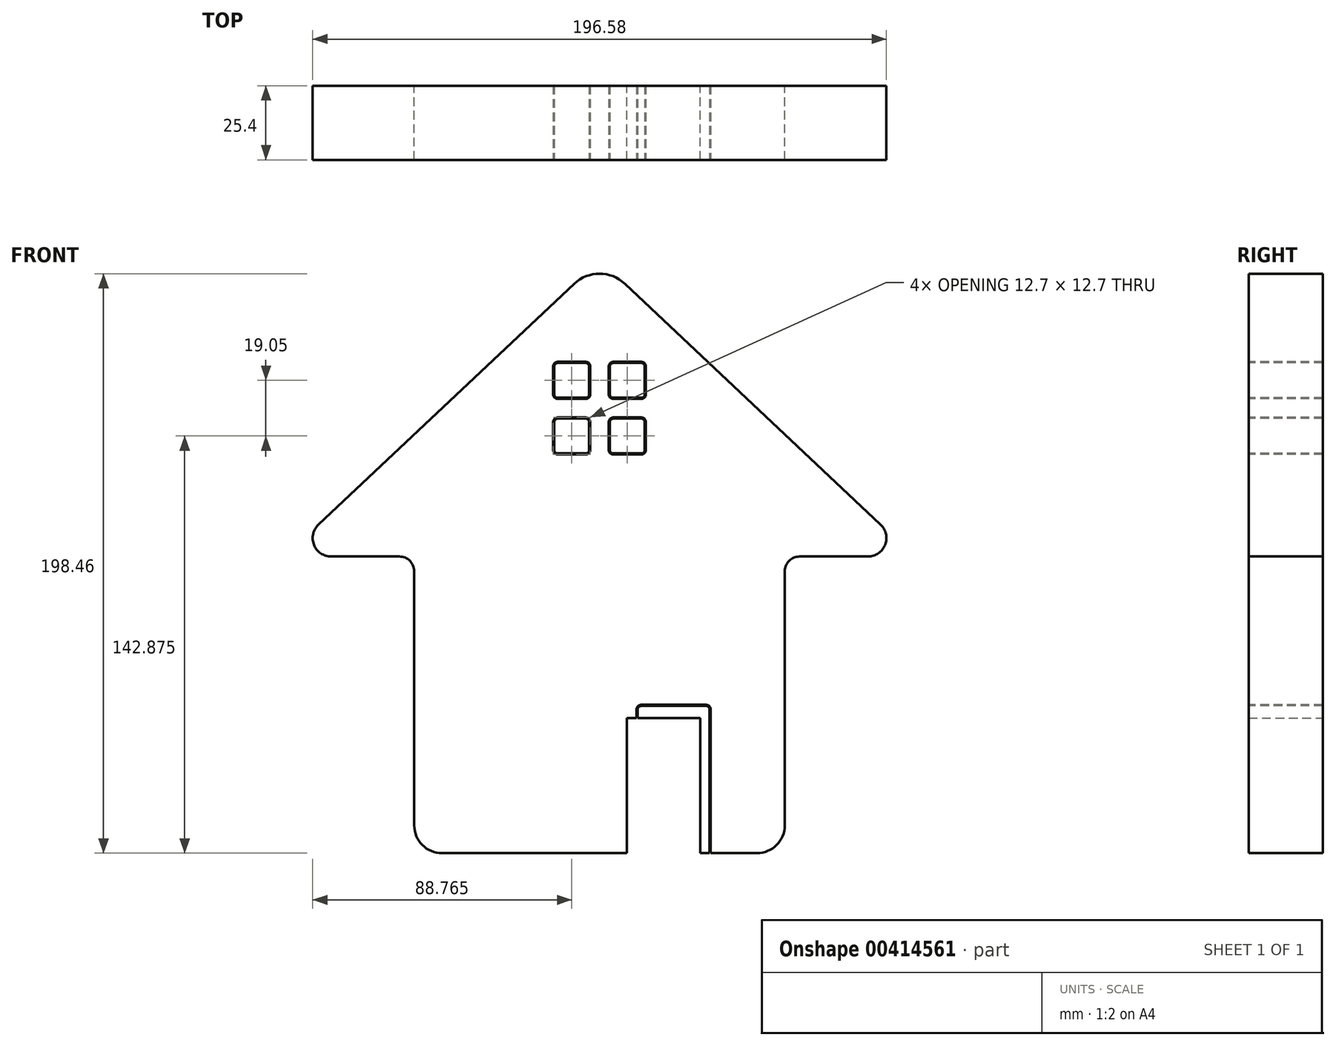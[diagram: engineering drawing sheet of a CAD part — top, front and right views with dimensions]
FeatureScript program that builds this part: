
annotation { "Feature Type Name" : "Feature", "Feature Type Description" : "" }
export const myFeature = defineFeature(function(context is Context, id is Id, definition is map)
    precondition{}
    {
        {
            var Q0;
            Q0=qCreatedBy(makeId("Front.planeOp"),FACE);
            var sketch = newSketch(context, id + "F0", { "sketchPlane" : qUnion([Q0])});
            skLineSegment(sketch, "E0.bottom", {"start": v(-63.5, 0) * mm, "end": v(63.5, 0) * mm});
            skLineSegment(sketch, "E0.top", {"start": v(-63.5, 101.6) * mm, "end": v(63.5, 101.6) * mm, "construction": true});
            skLineSegment(sketch, "E0.left", {"start": v(-63.5, 0) * mm, "end": v(-63.5, 101.6) * mm});
            skLineSegment(sketch, "E0.right", {"start": v(63.5, 0) * mm, "end": v(63.5, 101.6) * mm});
            skLineSegment(sketch, "E1", {"start": v(-63.5, 101.6) * mm, "end": v(-107.95, 101.6) * mm});
            skLineSegment(sketch, "E2", {"start": v(-107.95, 101.6) * mm, "end": v(0, 203.2) * mm});
            skLineSegment(sketch, "E3", {"start": v(0, 203.2) * mm, "end": v(107.95, 101.6) * mm});
            skLineSegment(sketch, "E4", {"start": v(107.95, 101.6) * mm, "end": v(63.5, 101.6) * mm});
            skLineSegment(sketch, "E5.bottom", {"start": v(9.41, 0) * mm, "end": v(34.5, 0) * mm});
            skLineSegment(sketch, "E5.top", {"start": v(9.41, 46.26) * mm, "end": v(34.5, 46.26) * mm});
            skLineSegment(sketch, "E5.left", {"start": v(9.41, 0) * mm, "end": v(9.41, 46.26) * mm});
            skLineSegment(sketch, "E5.right", {"start": v(34.5, 0) * mm, "end": v(34.5, 46.26) * mm});
            skSolve(sketch);
        }
        {
            var Q0;
            {var subQ1=sQuery(id+"F0.wireOp",EDGE,"E0.left");Q0=makeQuery(id+"F0.imprint","IMPRINT",FACE,{"disambiguationData":[TD([[makeQuery(id+"F0.imprint","IMPRINT",EDGE,{"derivedFrom":subQ1}),-1.0]])]});}
            var Q1;
            Q1=makeQuery(id+"F0.imprint","IMPRINT",FACE,{"disambiguationData":[TD([[makeQuery(id+"F0.imprint","IMPRINT",EDGE,{"derivedFrom":sQuery(id+"F0.wireOp",EDGE,"E5.bottom")}),1.0]])]});
            extrude(context, id + "F1", {"entities" : qUnion([Q0, Q1]), "depth" : 25.4 * mm});
        }
        {
            var Q0;
            Q0=makeQuery(id+"F1.opExtrude","CAP_FACE",FACE,{"disambiguationData":[OSD([sQuery(id+"F0.wireOp",EDGE,"E0.bottom"),sQuery(id+"F0.wireOp",EDGE,"E0.left"),sQuery(id+"F0.wireOp",EDGE,"E0.right"),sQuery(id+"F0.wireOp",EDGE,"E1"),sQuery(id+"F0.wireOp",EDGE,"E2"),sQuery(id+"F0.wireOp",EDGE,"E3"),sQuery(id+"F0.wireOp",EDGE,"E4"),sQuery(id+"F0.wireOp",EDGE,"E5.bottom")])],"isStart":false});
            var sketch = newSketch(context, id + "F2", { "sketchPlane" : qUnion([Q0])});
            skLineSegment(sketch, "E6.bottom", {"start": v(-19.05, 171.45) * mm, "end": v(19.05, 171.45) * mm, "construction": true});
            skLineSegment(sketch, "E6.top", {"start": v(-19.05, 133.35) * mm, "end": v(19.05, 133.35) * mm, "construction": true});
            skLineSegment(sketch, "E6.left", {"start": v(-19.05, 171.45) * mm, "end": v(-19.05, 133.35) * mm, "construction": true});
            skLineSegment(sketch, "E6.right", {"start": v(19.05, 171.45) * mm, "end": v(19.05, 133.35) * mm, "construction": true});
            skLineSegment(sketch, "E7", {"start": v(0, 203.2) * mm, "end": v(0, 171.45) * mm, "construction": true});
            skLineSegment(sketch, "E8.bottom", {"start": v(-14.29, 168.28) * mm, "end": v(-4.76, 168.28) * mm});
            skLineSegment(sketch, "E8.top", {"start": v(-14.29, 155.58) * mm, "end": v(-4.76, 155.58) * mm});
            skLineSegment(sketch, "E8.left", {"start": v(-15.88, 166.69) * mm, "end": v(-15.88, 157.16) * mm});
            skLineSegment(sketch, "E8.right", {"start": v(-3.18, 166.69) * mm, "end": v(-3.18, 157.16) * mm});
            skLineSegment(sketch, "E9.bottom", {"start": v(4.76, 168.28) * mm, "end": v(14.29, 168.28) * mm});
            skLineSegment(sketch, "E9.top", {"start": v(4.76, 155.58) * mm, "end": v(14.29, 155.58) * mm});
            skLineSegment(sketch, "E9.left", {"start": v(3.17, 166.69) * mm, "end": v(3.17, 157.16) * mm});
            skLineSegment(sketch, "E9.right", {"start": v(15.87, 166.69) * mm, "end": v(15.87, 157.16) * mm});
            skLineSegment(sketch, "E10.bottom", {"start": v(-14.29, 149.23) * mm, "end": v(-4.76, 149.23) * mm});
            skLineSegment(sketch, "E10.top", {"start": v(-14.29, 136.53) * mm, "end": v(-4.76, 136.53) * mm});
            skLineSegment(sketch, "E10.left", {"start": v(-15.88, 147.64) * mm, "end": v(-15.88, 138.11) * mm});
            skLineSegment(sketch, "E10.right", {"start": v(-3.18, 147.64) * mm, "end": v(-3.18, 138.11) * mm});
            skLineSegment(sketch, "E11.bottom", {"start": v(4.76, 149.23) * mm, "end": v(14.29, 149.23) * mm});
            skLineSegment(sketch, "E11.top", {"start": v(4.76, 136.53) * mm, "end": v(14.29, 136.53) * mm});
            skLineSegment(sketch, "E11.left", {"start": v(3.17, 147.64) * mm, "end": v(3.17, 138.11) * mm});
            skLineSegment(sketch, "E11.right", {"start": v(15.87, 147.64) * mm, "end": v(15.87, 138.11) * mm});
            skLineSegment(sketch, "E12", {"start": v(-3.17, 168.28) * mm, "end": v(3.17, 168.28) * mm, "construction": true});
            skLineSegment(sketch, "E13", {"start": v(0, 168.28) * mm, "end": v(0, 171.45) * mm, "construction": true});
            skLineSegment(sketch, "E14", {"start": v(-15.88, 168.28) * mm, "end": v(-15.88, 171.45) * mm});
            skLineSegment(sketch, "E15", {"start": v(-15.88, 136.53) * mm, "end": v(-15.88, 133.35) * mm});
            skPoint(sketch, "E16.visualSharp", {"position": v(-15.87, 168.28) * mm});
            skArc(sketch, "E16.filletArc", {"start": v(-14.29, 168.28) * mm, "mid": v(-15.41, 167.81) * mm, "end": v(-15.88, 166.69) * mm});
            skPoint(sketch, "E17.visualSharp", {"position": v(-3.17, 168.28) * mm});
            skArc(sketch, "E17.filletArc", {"start": v(-3.18, 166.69) * mm, "mid": v(-3.64, 167.81) * mm, "end": v(-4.76, 168.28) * mm});
            skPoint(sketch, "E18.visualSharp", {"position": v(-3.18, 155.58) * mm});
            skArc(sketch, "E18.filletArc", {"start": v(-4.76, 155.58) * mm, "mid": v(-3.64, 156.04) * mm, "end": v(-3.18, 157.16) * mm});
            skPoint(sketch, "E19.visualSharp", {"position": v(-15.88, 155.58) * mm});
            skArc(sketch, "E19.filletArc", {"start": v(-15.88, 157.16) * mm, "mid": v(-15.41, 156.04) * mm, "end": v(-14.29, 155.58) * mm});
            skPoint(sketch, "E20.visualSharp", {"position": v(3.17, 168.28) * mm});
            skArc(sketch, "E20.filletArc", {"start": v(4.76, 168.28) * mm, "mid": v(3.64, 167.81) * mm, "end": v(3.17, 166.69) * mm});
            skPoint(sketch, "E21.visualSharp", {"position": v(15.87, 168.28) * mm});
            skArc(sketch, "E21.filletArc", {"start": v(15.87, 166.69) * mm, "mid": v(15.41, 167.81) * mm, "end": v(14.29, 168.28) * mm});
            skPoint(sketch, "E22.visualSharp", {"position": v(15.87, 155.58) * mm});
            skArc(sketch, "E22.filletArc", {"start": v(14.29, 155.58) * mm, "mid": v(15.41, 156.04) * mm, "end": v(15.87, 157.16) * mm});
            skPoint(sketch, "E23.visualSharp", {"position": v(3.17, 155.58) * mm});
            skArc(sketch, "E23.filletArc", {"start": v(3.17, 157.16) * mm, "mid": v(3.64, 156.04) * mm, "end": v(4.76, 155.58) * mm});
            skPoint(sketch, "E24.visualSharp", {"position": v(-3.18, 149.23) * mm});
            skArc(sketch, "E24.filletArc", {"start": v(-3.18, 147.64) * mm, "mid": v(-3.64, 148.76) * mm, "end": v(-4.76, 149.23) * mm});
            skPoint(sketch, "E25.visualSharp", {"position": v(-15.88, 149.23) * mm});
            skArc(sketch, "E25.filletArc", {"start": v(-14.29, 149.23) * mm, "mid": v(-15.41, 148.76) * mm, "end": v(-15.88, 147.64) * mm});
            skPoint(sketch, "E26.visualSharp", {"position": v(-15.88, 136.53) * mm});
            skArc(sketch, "E26.filletArc", {"start": v(-15.88, 138.11) * mm, "mid": v(-15.41, 136.99) * mm, "end": v(-14.29, 136.53) * mm});
            skPoint(sketch, "E27.visualSharp", {"position": v(-3.17, 136.53) * mm});
            skArc(sketch, "E27.filletArc", {"start": v(-4.76, 136.53) * mm, "mid": v(-3.64, 136.99) * mm, "end": v(-3.18, 138.11) * mm});
            skPoint(sketch, "E28.visualSharp", {"position": v(3.17, 136.53) * mm});
            skArc(sketch, "E28.filletArc", {"start": v(3.17, 138.11) * mm, "mid": v(3.64, 136.99) * mm, "end": v(4.76, 136.53) * mm});
            skPoint(sketch, "E29.visualSharp", {"position": v(15.87, 136.53) * mm});
            skArc(sketch, "E29.filletArc", {"start": v(14.29, 136.53) * mm, "mid": v(15.41, 136.99) * mm, "end": v(15.87, 138.11) * mm});
            skPoint(sketch, "E30.visualSharp", {"position": v(15.87, 149.23) * mm});
            skArc(sketch, "E30.filletArc", {"start": v(15.87, 147.64) * mm, "mid": v(15.41, 148.76) * mm, "end": v(14.29, 149.23) * mm});
            skPoint(sketch, "E31.visualSharp", {"position": v(3.17, 149.23) * mm});
            skArc(sketch, "E31.filletArc", {"start": v(4.76, 149.23) * mm, "mid": v(3.64, 148.76) * mm, "end": v(3.17, 147.64) * mm});
            skSolve(sketch);
        }
        {
            var Q0;
            Q0=makeQuery(id+"F2.imprint","IMPRINT",FACE,{"disambiguationData":[TD([[makeQuery(id+"F2.imprint","IMPRINT",EDGE,{"derivedFrom":sQuery(id+"F2.wireOp",EDGE,"E9.bottom")}),-1.0]])]});
            var Q1;
            Q1=makeQuery(id+"F2.imprint","IMPRINT",FACE,{"disambiguationData":[TD([[makeQuery(id+"F2.imprint","IMPRINT",EDGE,{"derivedFrom":sQuery(id+"F2.wireOp",EDGE,"E10.bottom")}),-1.0]])]});
            var Q2;
            Q2=makeQuery(id+"F2.imprint","IMPRINT",FACE,{"disambiguationData":[TD([[makeQuery(id+"F2.imprint","IMPRINT",EDGE,{"derivedFrom":sQuery(id+"F2.wireOp",EDGE,"E11.bottom")}),-1.0]])]});
            var Q3;
            Q3=makeQuery(id+"F2.imprint","IMPRINT",FACE,{"disambiguationData":[TD([[makeQuery(id+"F2.imprint","IMPRINT",EDGE,{"derivedFrom":sQuery(id+"F2.wireOp",EDGE,"E8.bottom")}),-1.0]])]});
            extrude(context, id + "F3", {"entities" : qUnion([Q0, Q1, Q2, Q3]), "operationType" : NewBodyOperationType.REMOVE, "oppositeDirection" : true, "depth" : 25.4 * mm});
        }
        {
            var Q0;
            Q0=makeQuery(id+"F1.opExtrude","CAP_FACE",FACE,{"disambiguationData":[OSD([sQuery(id+"F0.wireOp",EDGE,"E0.bottom"),sQuery(id+"F0.wireOp",EDGE,"E0.left"),sQuery(id+"F0.wireOp",EDGE,"E0.right"),sQuery(id+"F0.wireOp",EDGE,"E1"),sQuery(id+"F0.wireOp",EDGE,"E2"),sQuery(id+"F0.wireOp",EDGE,"E3"),sQuery(id+"F0.wireOp",EDGE,"E4"),sQuery(id+"F0.wireOp",EDGE,"E5.bottom")])],"isStart":false});
            var sketch = newSketch(context, id + "F4", { "sketchPlane" : qUnion([Q0])});
            skArc(sketch, "E32.0", {"start": v(-14.29, 167.9) * mm, "mid": v(-15.14, 167.54) * mm, "end": v(-15.5, 166.69) * mm});
            skLineSegment(sketch, "E32.1", {"start": v(-15.5, 166.69) * mm, "end": v(-15.5, 157.16) * mm});
            skLineSegment(sketch, "E32.2", {"start": v(-14.29, 167.9) * mm, "end": v(-4.76, 167.9) * mm});
            skArc(sketch, "E32.3", {"start": v(-15.5, 157.16) * mm, "mid": v(-15.14, 156.3) * mm, "end": v(-14.29, 155.96) * mm});
            skArc(sketch, "E32.4", {"start": v(-3.56, 166.69) * mm, "mid": v(-3.9, 167.54) * mm, "end": v(-4.76, 167.9) * mm});
            skLineSegment(sketch, "E32.5", {"start": v(-3.56, 166.69) * mm, "end": v(-3.56, 157.16) * mm});
            skArc(sketch, "E32.6", {"start": v(-4.76, 155.96) * mm, "mid": v(-3.9, 156.3) * mm, "end": v(-3.56, 157.16) * mm});
            skLineSegment(sketch, "E32.7", {"start": v(-14.29, 155.96) * mm, "end": v(-4.76, 155.96) * mm});
            skArc(sketch, "E33.0", {"start": v(4.76, 167.9) * mm, "mid": v(3.9, 167.54) * mm, "end": v(3.56, 166.69) * mm});
            skLineSegment(sketch, "E33.1", {"start": v(3.56, 166.69) * mm, "end": v(3.56, 157.16) * mm});
            skLineSegment(sketch, "E33.2", {"start": v(4.76, 167.9) * mm, "end": v(14.29, 167.9) * mm});
            skArc(sketch, "E33.3", {"start": v(3.56, 157.16) * mm, "mid": v(3.9, 156.3) * mm, "end": v(4.76, 155.96) * mm});
            skArc(sketch, "E33.4", {"start": v(15.5, 166.69) * mm, "mid": v(15.14, 167.54) * mm, "end": v(14.29, 167.9) * mm});
            skLineSegment(sketch, "E33.5", {"start": v(15.5, 166.69) * mm, "end": v(15.5, 157.16) * mm});
            skArc(sketch, "E33.6", {"start": v(14.29, 155.96) * mm, "mid": v(15.14, 156.3) * mm, "end": v(15.5, 157.16) * mm});
            skLineSegment(sketch, "E33.7", {"start": v(4.76, 155.96) * mm, "end": v(14.29, 155.96) * mm});
            skArc(sketch, "E34.0", {"start": v(-14.29, 148.84) * mm, "mid": v(-15.14, 148.5) * mm, "end": v(-15.5, 147.64) * mm});
            skLineSegment(sketch, "E34.1", {"start": v(-15.5, 147.64) * mm, "end": v(-15.5, 138.11) * mm});
            skLineSegment(sketch, "E34.2", {"start": v(-14.29, 148.84) * mm, "end": v(-4.76, 148.84) * mm});
            skArc(sketch, "E34.3", {"start": v(-15.5, 138.11) * mm, "mid": v(-15.14, 137.26) * mm, "end": v(-14.29, 136.9) * mm});
            skArc(sketch, "E34.4", {"start": v(-3.56, 147.64) * mm, "mid": v(-3.9, 148.5) * mm, "end": v(-4.76, 148.84) * mm});
            skLineSegment(sketch, "E34.5", {"start": v(-3.56, 147.64) * mm, "end": v(-3.56, 138.11) * mm});
            skArc(sketch, "E34.6", {"start": v(-4.76, 136.9) * mm, "mid": v(-3.9, 137.26) * mm, "end": v(-3.56, 138.11) * mm});
            skLineSegment(sketch, "E34.7", {"start": v(-14.29, 136.9) * mm, "end": v(-4.76, 136.9) * mm});
            skArc(sketch, "E35.0", {"start": v(4.76, 148.84) * mm, "mid": v(3.9, 148.5) * mm, "end": v(3.56, 147.64) * mm});
            skLineSegment(sketch, "E35.1", {"start": v(3.56, 147.64) * mm, "end": v(3.56, 138.11) * mm});
            skLineSegment(sketch, "E35.2", {"start": v(4.76, 148.84) * mm, "end": v(14.29, 148.84) * mm});
            skArc(sketch, "E35.3", {"start": v(3.56, 138.11) * mm, "mid": v(3.9, 137.26) * mm, "end": v(4.76, 136.9) * mm});
            skArc(sketch, "E35.4", {"start": v(15.5, 147.64) * mm, "mid": v(15.14, 148.5) * mm, "end": v(14.29, 148.84) * mm});
            skLineSegment(sketch, "E35.5", {"start": v(15.5, 147.64) * mm, "end": v(15.5, 138.11) * mm});
            skArc(sketch, "E35.6", {"start": v(14.29, 136.9) * mm, "mid": v(15.14, 137.26) * mm, "end": v(15.5, 138.11) * mm});
            skLineSegment(sketch, "E35.7", {"start": v(4.76, 136.9) * mm, "end": v(14.29, 136.9) * mm});
            skSolve(sketch);
        }
        {
            var Q0;
            Q0=makeQuery(id+"F4.imprint","IMPRINT",FACE,{"disambiguationData":[TD([[makeQuery(id+"F4.imprint","IMPRINT",EDGE,{"derivedFrom":sQuery(id+"F4.wireOp",EDGE,"E32.0")}),1.0]])]});
            var Q1;
            Q1=makeQuery(id+"F4.imprint","IMPRINT",FACE,{"disambiguationData":[TD([[makeQuery(id+"F4.imprint","IMPRINT",EDGE,{"derivedFrom":sQuery(id+"F4.wireOp",EDGE,"E33.0")}),1.0]])]});
            var Q2;
            Q2=makeQuery(id+"F4.imprint","IMPRINT",FACE,{"disambiguationData":[TD([[makeQuery(id+"F4.imprint","IMPRINT",EDGE,{"derivedFrom":sQuery(id+"F4.wireOp",EDGE,"E34.0")}),1.0]])]});
            var Q3;
            Q3=makeQuery(id+"F4.imprint","IMPRINT",FACE,{"disambiguationData":[TD([[makeQuery(id+"F4.imprint","IMPRINT",EDGE,{"derivedFrom":sQuery(id+"F4.wireOp",EDGE,"E35.0")}),1.0]])]});
            extrude(context, id + "F5", {"entities" : qUnion([Q0, Q1, Q2, Q3]), "oppositeDirection" : true, "depth" : 25.4 * mm});
        }
        {
            var Q0;
            Q0=makeQuery(id+"F1.opExtrude","CAP_FACE",FACE,{"disambiguationData":[OSD([sQuery(id+"F0.wireOp",EDGE,"E0.bottom"),sQuery(id+"F0.wireOp",EDGE,"E0.left"),sQuery(id+"F0.wireOp",EDGE,"E0.right"),sQuery(id+"F0.wireOp",EDGE,"E1"),sQuery(id+"F0.wireOp",EDGE,"E2"),sQuery(id+"F0.wireOp",EDGE,"E3"),sQuery(id+"F0.wireOp",EDGE,"E4"),sQuery(id+"F0.wireOp",EDGE,"E5.bottom")])],"isStart":false});
            var sketch = newSketch(context, id + "F6", { "sketchPlane" : qUnion([Q0])});
            skLineSegment(sketch, "E36.bottom", {"start": v(12.7, 0) * mm, "end": v(38.1, 0) * mm});
            skLineSegment(sketch, "E36.top", {"start": v(14.29, 50.8) * mm, "end": v(36.51, 50.8) * mm});
            skLineSegment(sketch, "E36.left", {"start": v(12.7, 0) * mm, "end": v(12.7, 49.21) * mm});
            skLineSegment(sketch, "E36.right", {"start": v(38.1, 0) * mm, "end": v(38.1, 49.21) * mm});
            skPoint(sketch, "E37.visualSharp", {"position": v(12.7, 50.8) * mm});
            skArc(sketch, "E37.filletArc", {"start": v(14.29, 50.8) * mm, "mid": v(13.16, 50.34) * mm, "end": v(12.7, 49.21) * mm});
            skPoint(sketch, "E38.visualSharp", {"position": v(38.1, 50.8) * mm});
            skArc(sketch, "E38.filletArc", {"start": v(38.1, 49.21) * mm, "mid": v(37.64, 50.34) * mm, "end": v(36.51, 50.8) * mm});
            skLineSegment(sketch, "E39.0", {"start": v(37.72, 0) * mm, "end": v(37.72, 49.21) * mm});
            skLineSegment(sketch, "E39.1", {"start": v(13.08, 0) * mm, "end": v(13.08, 49.21) * mm});
            skArc(sketch, "E39.2", {"start": v(14.29, 50.42) * mm, "mid": v(13.43, 50.07) * mm, "end": v(13.08, 49.21) * mm});
            skLineSegment(sketch, "E39.3", {"start": v(14.29, 50.42) * mm, "end": v(36.51, 50.42) * mm});
            skArc(sketch, "E39.4", {"start": v(37.72, 49.21) * mm, "mid": v(37.37, 50.07) * mm, "end": v(36.51, 50.42) * mm});
            skSolve(sketch);
        }
        {
            var Q0;
            Q0=makeQuery(id+"F6.imprint","IMPRINT",FACE,{"disambiguationData":[TD([[makeQuery(id+"F6.imprint","IMPRINT",EDGE,{"derivedFrom":sQuery(id+"F6.wireOp",EDGE,"E36.top")}),-1.0]])]});
            extrude(context, id + "F7", {"entities" : qUnion([Q0]), "operationType" : NewBodyOperationType.REMOVE, "oppositeDirection" : true, "depth" : 25.4 * mm});
        }
        {
            var Q0;
            Q0=makeQuery(id+"F1.opExtrude","SWEPT_EDGE",EDGE,{"disambiguationData":[OSD([sQuery(id+"F0.wireOp",EDGE,"E3"),sQuery(id+"F0.wireOp",EDGE,"E4")])]});
            var Q1;
            Q1=makeQuery(id+"F1.opExtrude","SWEPT_EDGE",EDGE,{"disambiguationData":[OSD([sQuery(id+"F0.wireOp",EDGE,"E1"),sQuery(id+"F0.wireOp",EDGE,"E2")])]});
            fillet(context, id + "F8", {"entities" : qUnion([Q0, Q1]), "radius" : 6.35 * mm, "tangentPropagation" : true, "allowEdgeOverflow" : false});
        }
        {
            var Q0;
            Q0=makeQuery(id+"F1.opExtrude","SWEPT_EDGE",EDGE,{"disambiguationData":[OSD([sQuery(id+"F0.wireOp",EDGE,"E2"),sQuery(id+"F0.wireOp",EDGE,"E3")])]});
            fillet(context, id + "F9", {"entities" : qUnion([Q0]), "radius" : 12.7 * mm, "tangentPropagation" : true, "allowEdgeOverflow" : false});
        }
        {
            var Q0;
            Q0=makeQuery(id+"F1.opExtrude","SWEPT_EDGE",EDGE,{"disambiguationData":[OSD([sQuery(id+"F0.wireOp",EDGE,"E0.bottom"),sQuery(id+"F0.wireOp",EDGE,"E0.right")])]});
            var Q1;
            Q1=makeQuery(id+"F1.opExtrude","SWEPT_EDGE",EDGE,{"disambiguationData":[OSD([sQuery(id+"F0.wireOp",EDGE,"E0.bottom"),sQuery(id+"F0.wireOp",EDGE,"E0.left")])]});
            fillet(context, id + "F10", {"entities" : qUnion([Q0, Q1]), "radius" : 9.52 * mm, "tangentPropagation" : true, "allowEdgeOverflow" : false});
        }
        {
            var Q0;
            Q0=makeQuery(id+"F1.opExtrude","SWEPT_EDGE",EDGE,{"disambiguationData":[OSD([sQuery(id+"F0.wireOp",EDGE,"E0.left"),sQuery(id+"F0.wireOp",EDGE,"E1")])]});
            var Q1;
            Q1=makeQuery(id+"F1.opExtrude","SWEPT_EDGE",EDGE,{"disambiguationData":[OSD([sQuery(id+"F0.wireOp",EDGE,"E0.right"),sQuery(id+"F0.wireOp",EDGE,"E4")])]});
            fillet(context, id + "F11", {"entities" : qUnion([Q0, Q1]), "radius" : 5.08 * mm, "tangentPropagation" : true, "allowEdgeOverflow" : false});
        }
    });
